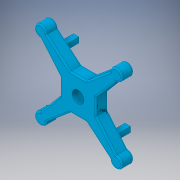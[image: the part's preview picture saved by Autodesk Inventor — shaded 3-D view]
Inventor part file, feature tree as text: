
AUTODESK INVENTOR PART (.ipt)
format: ipt  version: 2019 (Build 230136000, 136)  size: 264,704 bytes
history: native  units: in
note: dims shown in document units (in); Inventor stores cm internally (conversion verified against a paired STEP export)
features: sketch x5, extrude x2, fillet x2, pattern_circular x1
ambient origin geometry x8: Origin, YZ Plane, XZ Plane, XY Plane, X Axis, Y Axis, Z Axis, Center Point
bodies: Solid1 (feature_tree)
feature tree (10):
  extrude  "Extrusion1"  Depth=1.0in
  fillet  "Fillet1"  Radius=0.125in
  sketch  "Sketch2"  dims[d4=0.6875in d5=3.0in]
  fillet  "Fillet2"  Radius=1.0in
  sketch  "Sketch3"  dims[d6=0.6875in]
  sketch  "Sketch4"  dims[d7=1.0in d8=1.5748in d10=360.0deg]
  extrude  "Extrusion3"  Depth=3.0in
  pattern_circular  "Circular Pattern2"  Count=4 Angle=360.0deg
  sketch  "Sketch1"  dims[d0=3.0in d1=3.0in d2=0.125in d3=1.0in]
  sketch  "Sketch5"  dims[d12=1.0in d13=0.0in d14=0.125in d15=0.125in d16=0.75in d23=1.0in d24=0.0in d25=1.5748in d26=360.0deg]
